# Revit family: Hager-Univers-IP44-D161-H1100-Cl.II-FWQ_encl-NL-en
name_source: partatom
category: Equipement électrique
units: mm (PartAtom-declared; Revit-internal decimal feet)

## family parameters
Configuration du panneau = Deux colonnes, circuits au sein
Cote de connecteur circulaire = Utiliser le diamètre
Couper avec des vides une fois chargée = Non
Hôte = Face
Partagée = Non
Point de calcul de pièce = Non
Type d'élément = Tableau de raccordement

## types (4) — shared parameters
Commentaires du type = Univers
EF000003 - Mounting method = EV000384 - Surface mounted (plaster)
EF000007 - Colour = EV000202 - White
EF000040 - Height = 1100 mm
EF000049 - Depth = 161 mm  [stored 0.528215 ft]
EF000116 - RAL-number = 9010
EF000118 - With mounting plate = Oui
EF000339 - Type of cover = EV001012 - Cover
EF001088 - Extension possible = Oui
EF001131 - Internal depth = 161 mm  [stored 0.528215 ft]
EF001596 - Material housing = EV000179 - Steel
EF001613 - Circuit integrity = EV000494 - None
EF002950 - Width in number of modular spacings = 12
EF003532 - Suitable for outdoor use = Non
EF004293 - Impact strength = EV006815 - IK09
EF004464 - Type of door = EV002646 - Single
EF005474 - Degree of protection (IP) = EV006418 - IP44
EF006244 - Transparent cover/door = Non
EF006306 - With lock = Non
EF007800 - Suitable for lightning protection = Non
EF008873 - Nominal current (In) = 125 A
EF009170 - Material plate thickness cabinet = 2 mm  [stored 0.00656168 ft]
EF009171 - Material plate thickness door/cover = 2 mm  [stored 0.00656168 ft]
EF009212 - Cover model = EV009916 - With notch
EF015940 - Cover with overpressure release = Non
Fabricant = Hager
HG000002 - With door or cover = Oui
HG000003 - Range = Univers
HG000006 - Flush mounted = Non
HG000023 - Double section enclosure = Non
HG000024 - Bottom section height = 800 mm  [stored 2.62467 ft]
HG000026 - Floor standing = Non
zero-valued in all types: EF000218 - Built-in depth, Elévation par défaut, HG000027 - Plinth height

## per-type parameters (varying)
| type | EF000008 - Width | EF000266 - Number of rows | EF000437 - Number of conduit inlets | EF004427 - Number of modules | EF009554 - Number of openings for flange plates | HG000004 - Manufacturer reference | HG000009 - Double swing door | HG000010 - Asymmetric doors |
| Surface mounted (plaster) IP44 W1050 H1100 D161  - FWQ74P | 1050 mm | 28 | 16 | 336 | 8 | FWQ74P | Oui | Non |
| Surface mounted (plaster) IP44 W300 H1100 D161  - FWQ71P | 300 mm | 1 | 4 | 84 | 2 | FWQ71P | Non | Non |
| Surface mounted (plaster) IP44 W550 H1100 D161  - FWQ72P | 550 mm | 14 | 8 | 168 | 4 | FWQ72P | Non | Non |
| Surface mounted (plaster) IP44 W800 H1100 D161  - FWQ73P | 800 mm  [stored 2.62467 ft] | 21 | 12 | 252 | 6 | FWQ73P | Oui | Oui |

note: [stored X ft] marks values corroborated as IEEE doubles in the binary element streams (Revit-internal decimal feet)

## geometry (parser evidence)
native form markers: Sweep x7
no freeform markers — native parametric forms only
